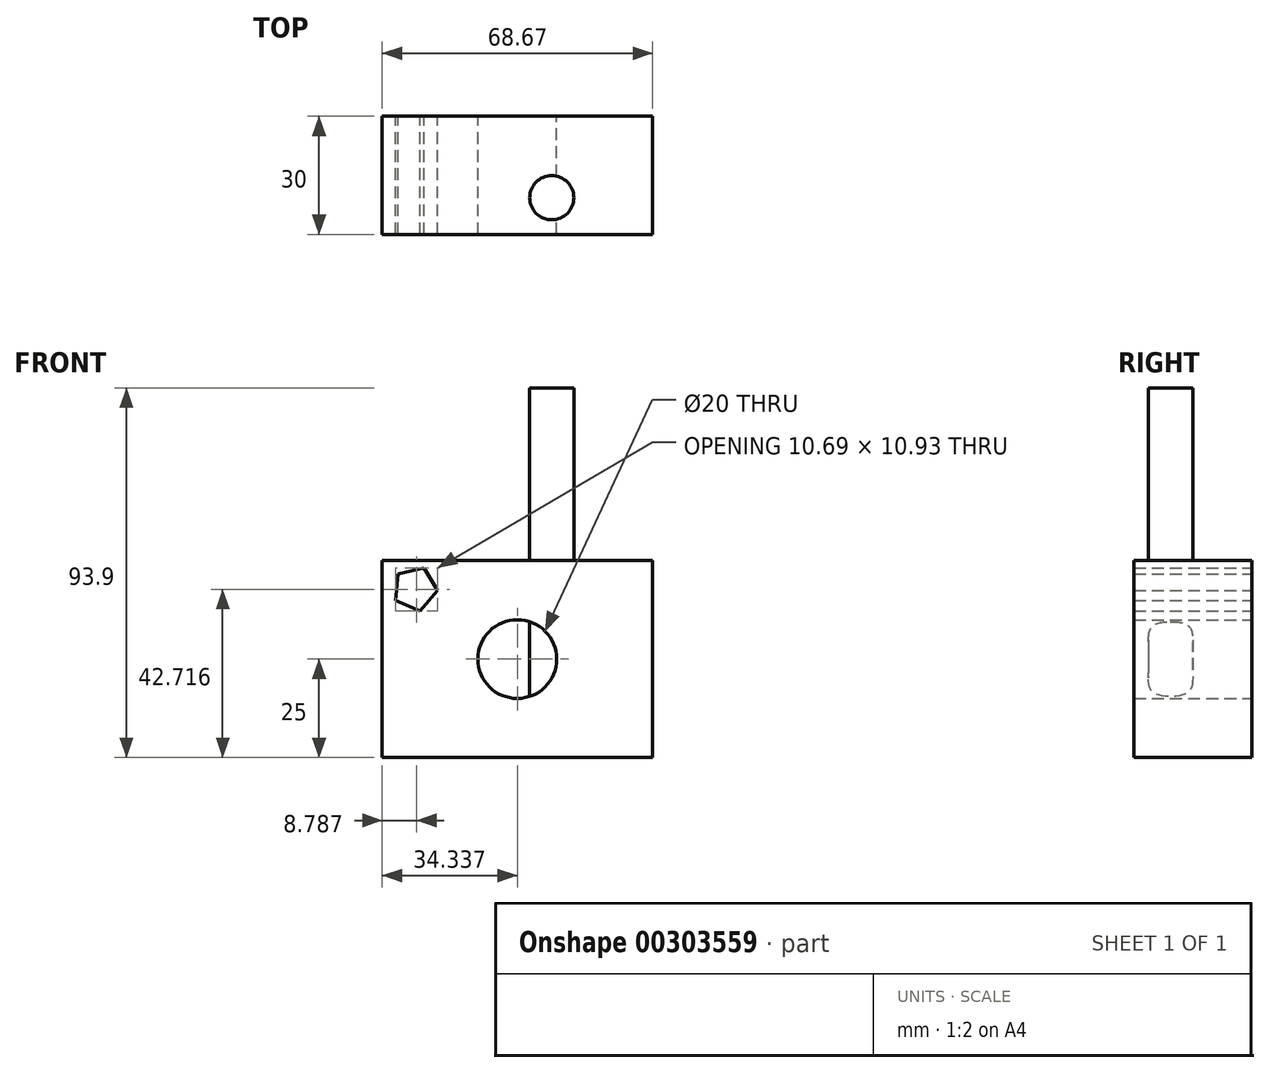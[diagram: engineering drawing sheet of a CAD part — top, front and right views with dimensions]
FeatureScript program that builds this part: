
annotation { "Feature Type Name" : "Feature", "Feature Type Description" : "" }
export const myFeature = defineFeature(function(context is Context, id is Id, definition is map)
    precondition{}
    {
        {
            var Q0;
            Q0=qCreatedBy(makeId("Front.planeOp"),FACE);
            var sketch = newSketch(context, id + "F0", { "sketchPlane" : qUnion([Q0])});
            skLineSegment(sketch, "E0.bottom", {"start": v(0, 0) * mm, "end": v(68.67, 0) * mm});
            skLineSegment(sketch, "E0.top", {"start": v(0, 50) * mm, "end": v(68.67, 50) * mm});
            skLineSegment(sketch, "E0.left", {"start": v(0, 0) * mm, "end": v(0, 50) * mm});
            skLineSegment(sketch, "E0.right", {"start": v(68.67, 0) * mm, "end": v(68.67, 50) * mm});
            skCircle(sketch, "E1", {"center": v(34.34, 25) * mm, "radius": 10 * mm});
            skPoint(sketch, "E1.centerSnap0", {"position": v(68.67, 25) * mm});
            skPoint(sketch, "E1.centerSnap1", {"position": v(34.34, 50) * mm});
            skCircle(sketch, "E2.cCircle", {"center": v(8.38, 42.87) * mm, "radius": 4.67 * mm, "construction": true});
            skLineSegment(sketch, "E2.0", {"start": v(14.13, 42.37) * mm, "end": v(9.69, 37.25) * mm});
            skLineSegment(sketch, "E2.1", {"start": v(9.69, 37.25) * mm, "end": v(3.44, 39.9) * mm});
            skLineSegment(sketch, "E2.2", {"start": v(3.44, 39.9) * mm, "end": v(4.02, 46.65) * mm});
            skLineSegment(sketch, "E2.3", {"start": v(4.02, 46.65) * mm, "end": v(10.63, 48.18) * mm});
            skLineSegment(sketch, "E2.4", {"start": v(10.63, 48.18) * mm, "end": v(14.13, 42.37) * mm});
            skPoint(sketch, "E2.0.midPoint", {"position": v(11.91, 39.81) * mm});
            skLineSegment(sketch, "E3", {"start": v(0, 55.57) * mm, "end": v(68.67, 0) * mm, "construction": true});
            skLineSegment(sketch, "E4", {"start": v(0, 55.57) * mm, "end": v(0, 50) * mm});
            skPoint(sketch, "E5.center", {"position": v(0, 0) * mm});
            skSolve(sketch);
        }
        {
            var Q0;
            Q0 = qSketchRegion(id + "F0", true);
            extrude(context, id + "F1", {"entities" : qUnion([Q0]), "endBound" : BoundingType.SYMMETRIC, "depth" : 30 * mm});
        }
        {
            var Q0;
            Q0=makeQuery(id+"F1.opExtrude","SWEPT_FACE",FACE,{"disambiguationData":[OSD([sQuery(id+"F0.wireOp",EDGE,"E0.bottom")])]});
            var sketch = newSketch(context, id + "F2", { "sketchPlane" : qUnion([Q0])});
            skCircle(sketch, "E6", {"center": v(43.1, 5.68) * mm, "radius": 5.6 * mm});
            skSolve(sketch);
        }
        {
            var Q0;
            Q0 = qSketchRegion(id + "F2", true);
            extrude(context, id + "F3", {"entities" : qUnion([Q0]), "operationType" : NewBodyOperationType.ADD, "oppositeDirection" : true, "depth" : 93.9 * mm});
        }
    });
